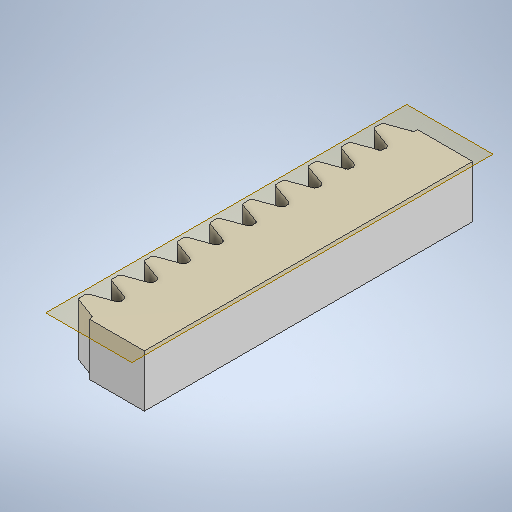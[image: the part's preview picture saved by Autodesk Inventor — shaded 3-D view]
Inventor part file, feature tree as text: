
AUTODESK INVENTOR PART (.ipt)
format: ipt  version: 2025.2 (Build 292293000, 293)  size: 334,336 bytes
history: native  units: mm
features: other x3, sketch x3, extrude x2, fillet x1, chamfer x1, pattern_linear x1
ambient origin geometry x8: Origin, YZ Plane, XZ Plane, XY Plane, X Axis, Y Axis, Z Axis, Center Point
bodies: Body1 (feature_tree)
feature tree (11):
  other  "ソリッド1"
  sketch  "スケッチ1"
  extrude  "押し出し1"  Depth=10.0mm TaperAngle=0.0deg
  other  "作業平面1"
  extrude  "押し出し2"  Depth=7.5mm
  fillet  "フィレット1"  [1 undecoded]
  chamfer  "面取り1"  Distance=5.0mm
  pattern_linear  "矩形状パターン1"  Spacing1=0.0mm  [1 undecoded]
  other  "2D 計算式曲線1"
  sketch  "スケッチ2"
  sketch  "スケッチ3"
note: 2 required parameter values undecoded (feature->parameter linkage not recoverable at this tier; creation-order binding heuristic only, values carry confidence <= 0.55)
